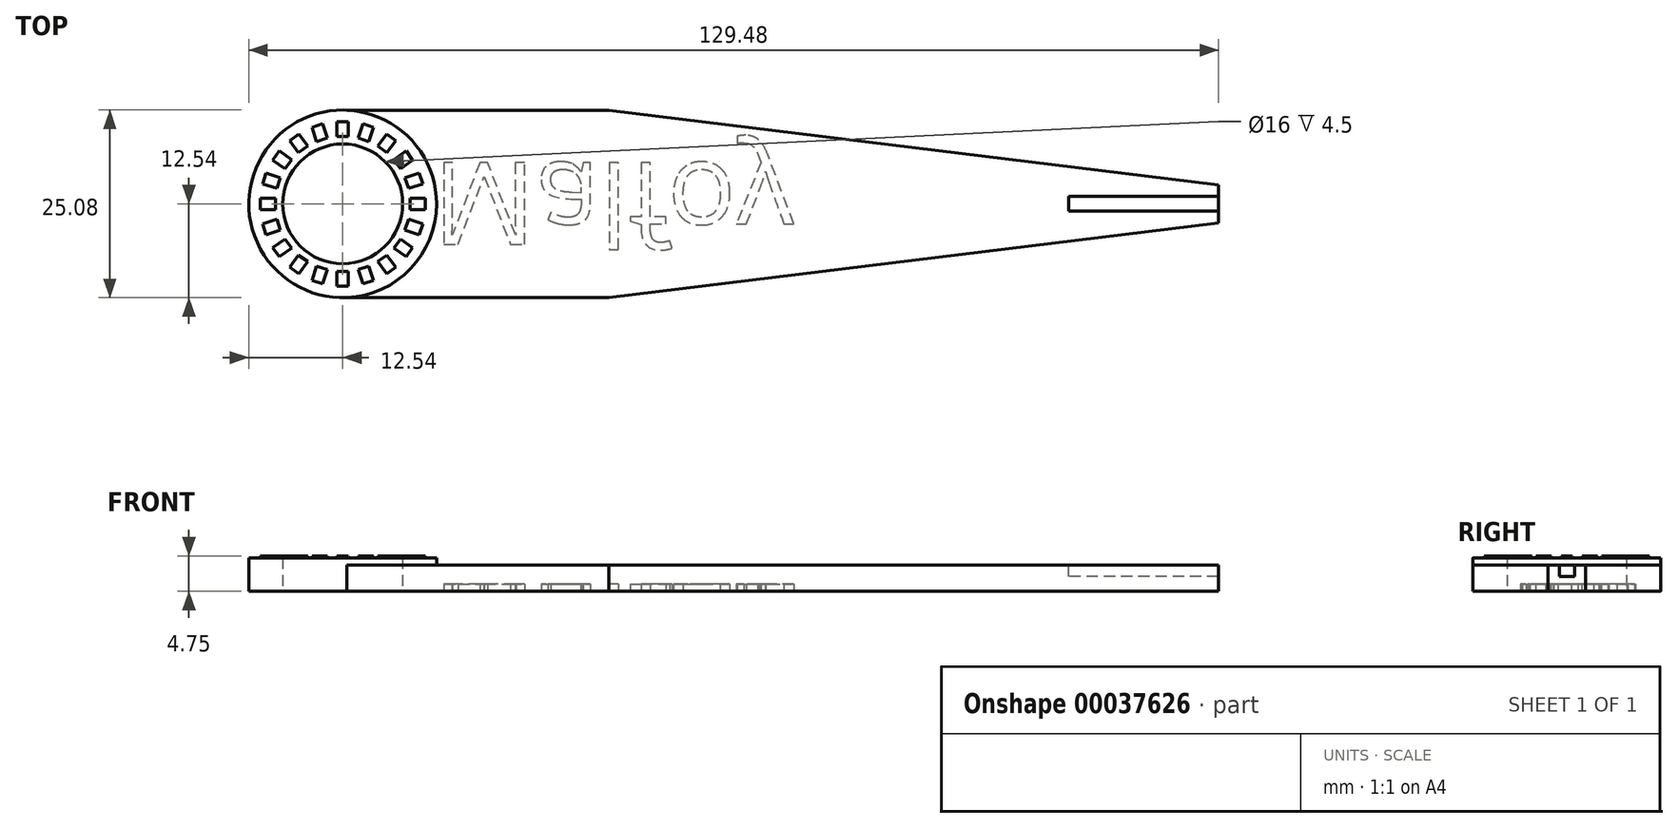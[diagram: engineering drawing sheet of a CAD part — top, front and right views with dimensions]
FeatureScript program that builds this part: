
annotation { "Feature Type Name" : "Feature", "Feature Type Description" : "" }
export const myFeature = defineFeature(function(context is Context, id is Id, definition is map)
    precondition{}
    {
        {
            var Q0;
            Q0=qCreatedBy(makeId("Top.planeOp"),FACE);
            var sketch = newSketch(context, id + "F0", { "sketchPlane" : qUnion([Q0])});
            skCircle(sketch, "E0", {"center": v(0, 0) * mm, "radius": 8 * mm});
            skLineSegment(sketch, "E1", {"start": v(35.56, 12.52) * mm, "end": v(0.56, 12.52) * mm});
            skPoint(sketch, "E2", {"position": v(0.56, 12.52) * mm});
            skLineSegment(sketch, "E3", {"start": v(0, 0) * mm, "end": v(47.57, 0) * mm, "construction": true});
            skLineSegment(sketch, "E4.MirrorCS", {"start": v(35.56, -12.52) * mm, "end": v(0.56, -12.52) * mm});
            skLineSegment(sketch, "E5", {"start": v(35.56, 12.52) * mm, "end": v(73.25, 12.52) * mm, "construction": true});
            skLineSegment(sketch, "E6", {"start": v(35.56, 12.52) * mm, "end": v(116.94, 2.53) * mm});
            skLineSegment(sketch, "E7.MirrorCS", {"start": v(35.56, -12.52) * mm, "end": v(116.94, -2.53) * mm});
            skLineSegment(sketch, "E8", {"start": v(116.94, 2.53) * mm, "end": v(116.94, -2.53) * mm});
            skArc(sketch, "E9", {"start": v(0.56, 12.52) * mm, "mid": v(-12.54, 0) * mm, "end": v(0.56, -12.52) * mm});
            skSolve(sketch);
        }
        {
            var Q0;
            Q0 = qSketchRegion(id + "F0", true);
            extrude(context, id + "F1", {"entities" : qUnion([Q0]), "depth" : 3.5 * mm});
        }
        {
            var Q0;
            Q0=makeQuery(id+"F1.opExtrude","CAP_FACE",FACE,{"disambiguationData":[OSD([sQuery(id+"F0.wireOp",EDGE,"E0"),sQuery(id+"F0.wireOp",EDGE,"E1"),sQuery(id+"F0.wireOp",EDGE,"E4.MirrorCS"),sQuery(id+"F0.wireOp",EDGE,"E6"),sQuery(id+"F0.wireOp",EDGE,"E7.MirrorCS"),sQuery(id+"F0.wireOp",EDGE,"E8"),sQuery(id+"F0.wireOp",EDGE,"E9")])],"isStart":false});
            var sketch = newSketch(context, id + "F2", { "sketchPlane" : qUnion([Q0])});
            skCircle(sketch, "E10", {"center": v(0, 0) * mm, "radius": 8 * mm});
            skCircle(sketch, "E11", {"center": v(0, 0) * mm, "radius": 12.54 * mm});
            skSolve(sketch);
        }
        {
            var Q0;
            Q0=makeQuery(id+"F2.imprint","IMPRINT",FACE,{"disambiguationData":[TD([[makeQuery(id+"F2.imprint","IMPRINT",EDGE,{"derivedFrom":sQuery(id+"F2.wireOp",EDGE,"E10")}),-1.0]])]});
            extrude(context, id + "F3", {"entities" : qUnion([Q0]), "operationType" : NewBodyOperationType.ADD, "depth" : 1 * mm});
        }
        {
            var Q0;
            Q0=makeQuery(id+"F3.opExtrude","CAP_FACE",FACE,{"disambiguationData":[OSD([sQuery(id+"F2.wireOp",EDGE,"E10"),sQuery(id+"F2.wireOp",EDGE,"E11")])],"isStart":false});
            var sketch = newSketch(context, id + "F4", { "sketchPlane" : qUnion([Q0])});
            skLineSegment(sketch, "E12.bottom", {"start": v(-0.75, 11) * mm, "end": v(0.75, 11) * mm});
            skLineSegment(sketch, "E12.top", {"start": v(-0.75, 9) * mm, "end": v(0.75, 9) * mm});
            skLineSegment(sketch, "E12.left", {"start": v(-0.75, 11) * mm, "end": v(-0.75, 9) * mm});
            skLineSegment(sketch, "E12.right", {"start": v(0.75, 11) * mm, "end": v(0.75, 9) * mm});
            skPoint(sketch, "E13", {"position": v(0, 8) * mm});
            skLineSegment(sketch, "E14.1.0", {"start": v(-4.11, 10.23) * mm, "end": v(-2.69, 10.7) * mm});
            skLineSegment(sketch, "E14.1.1", {"start": v(-4.11, 10.23) * mm, "end": v(-3.5, 8.33) * mm});
            skLineSegment(sketch, "E14.1.2", {"start": v(-3.5, 8.33) * mm, "end": v(-2.07, 8.8) * mm});
            skLineSegment(sketch, "E14.1.3", {"start": v(-2.69, 10.7) * mm, "end": v(-2.07, 8.8) * mm});
            skLineSegment(sketch, "E14.2.0", {"start": v(-7.07, 8.46) * mm, "end": v(-5.86, 9.34) * mm});
            skLineSegment(sketch, "E14.2.1", {"start": v(-7.07, 8.46) * mm, "end": v(-5.9, 6.84) * mm});
            skLineSegment(sketch, "E14.2.2", {"start": v(-5.9, 6.84) * mm, "end": v(-4.68, 7.72) * mm});
            skLineSegment(sketch, "E14.2.3", {"start": v(-5.86, 9.34) * mm, "end": v(-4.68, 7.72) * mm});
            skLineSegment(sketch, "E14.3.0", {"start": v(-9.34, 5.86) * mm, "end": v(-8.46, 7.07) * mm});
            skLineSegment(sketch, "E14.3.1", {"start": v(-9.34, 5.86) * mm, "end": v(-7.72, 4.68) * mm});
            skLineSegment(sketch, "E14.3.2", {"start": v(-7.72, 4.68) * mm, "end": v(-6.84, 5.9) * mm});
            skLineSegment(sketch, "E14.3.3", {"start": v(-8.46, 7.07) * mm, "end": v(-6.84, 5.9) * mm});
            skLineSegment(sketch, "E14.4.0", {"start": v(-10.7, 2.69) * mm, "end": v(-10.23, 4.11) * mm});
            skLineSegment(sketch, "E14.4.1", {"start": v(-10.7, 2.69) * mm, "end": v(-8.8, 2.07) * mm});
            skLineSegment(sketch, "E14.4.2", {"start": v(-8.8, 2.07) * mm, "end": v(-8.33, 3.5) * mm});
            skLineSegment(sketch, "E14.4.3", {"start": v(-10.23, 4.11) * mm, "end": v(-8.33, 3.5) * mm});
            skLineSegment(sketch, "E14.5.0", {"start": v(-11, -0.75) * mm, "end": v(-11, 0.75) * mm});
            skLineSegment(sketch, "E14.5.1", {"start": v(-11, -0.75) * mm, "end": v(-9, -0.75) * mm});
            skLineSegment(sketch, "E14.5.2", {"start": v(-9, -0.75) * mm, "end": v(-9, 0.75) * mm});
            skLineSegment(sketch, "E14.5.3", {"start": v(-11, 0.75) * mm, "end": v(-9, 0.75) * mm});
            skLineSegment(sketch, "E14.6.0", {"start": v(-10.23, -4.11) * mm, "end": v(-10.7, -2.69) * mm});
            skLineSegment(sketch, "E14.6.1", {"start": v(-10.23, -4.11) * mm, "end": v(-8.33, -3.5) * mm});
            skLineSegment(sketch, "E14.6.2", {"start": v(-8.33, -3.5) * mm, "end": v(-8.8, -2.07) * mm});
            skLineSegment(sketch, "E14.6.3", {"start": v(-10.7, -2.69) * mm, "end": v(-8.8, -2.07) * mm});
            skLineSegment(sketch, "E14.7.0", {"start": v(-8.46, -7.07) * mm, "end": v(-9.34, -5.86) * mm});
            skLineSegment(sketch, "E14.7.1", {"start": v(-8.46, -7.07) * mm, "end": v(-6.84, -5.9) * mm});
            skLineSegment(sketch, "E14.7.2", {"start": v(-6.84, -5.9) * mm, "end": v(-7.72, -4.68) * mm});
            skLineSegment(sketch, "E14.7.3", {"start": v(-9.34, -5.86) * mm, "end": v(-7.72, -4.68) * mm});
            skLineSegment(sketch, "E14.8.0", {"start": v(-5.86, -9.34) * mm, "end": v(-7.07, -8.46) * mm});
            skLineSegment(sketch, "E14.8.1", {"start": v(-5.86, -9.34) * mm, "end": v(-4.68, -7.72) * mm});
            skLineSegment(sketch, "E14.8.2", {"start": v(-4.68, -7.72) * mm, "end": v(-5.9, -6.84) * mm});
            skLineSegment(sketch, "E14.8.3", {"start": v(-7.07, -8.46) * mm, "end": v(-5.9, -6.84) * mm});
            skLineSegment(sketch, "E14.9.0", {"start": v(-2.69, -10.7) * mm, "end": v(-4.11, -10.23) * mm});
            skLineSegment(sketch, "E14.9.1", {"start": v(-2.69, -10.7) * mm, "end": v(-2.07, -8.8) * mm});
            skLineSegment(sketch, "E14.9.2", {"start": v(-2.07, -8.8) * mm, "end": v(-3.5, -8.33) * mm});
            skLineSegment(sketch, "E14.9.3", {"start": v(-4.11, -10.23) * mm, "end": v(-3.5, -8.33) * mm});
            skLineSegment(sketch, "E14.10.0", {"start": v(0.75, -11) * mm, "end": v(-0.75, -11) * mm});
            skLineSegment(sketch, "E14.10.1", {"start": v(0.75, -11) * mm, "end": v(0.75, -9) * mm});
            skLineSegment(sketch, "E14.10.2", {"start": v(0.75, -9) * mm, "end": v(-0.75, -9) * mm});
            skLineSegment(sketch, "E14.10.3", {"start": v(-0.75, -11) * mm, "end": v(-0.75, -9) * mm});
            skLineSegment(sketch, "E14.11.0", {"start": v(4.11, -10.23) * mm, "end": v(2.69, -10.7) * mm});
            skLineSegment(sketch, "E14.11.1", {"start": v(4.11, -10.23) * mm, "end": v(3.5, -8.33) * mm});
            skLineSegment(sketch, "E14.11.2", {"start": v(3.5, -8.33) * mm, "end": v(2.07, -8.8) * mm});
            skLineSegment(sketch, "E14.11.3", {"start": v(2.69, -10.7) * mm, "end": v(2.07, -8.8) * mm});
            skLineSegment(sketch, "E14.12.0", {"start": v(7.07, -8.46) * mm, "end": v(5.86, -9.34) * mm});
            skLineSegment(sketch, "E14.12.1", {"start": v(7.07, -8.46) * mm, "end": v(5.9, -6.84) * mm});
            skLineSegment(sketch, "E14.12.2", {"start": v(5.9, -6.84) * mm, "end": v(4.68, -7.72) * mm});
            skLineSegment(sketch, "E14.12.3", {"start": v(5.86, -9.34) * mm, "end": v(4.68, -7.72) * mm});
            skLineSegment(sketch, "E14.13.0", {"start": v(9.34, -5.86) * mm, "end": v(8.46, -7.07) * mm});
            skLineSegment(sketch, "E14.13.1", {"start": v(9.34, -5.86) * mm, "end": v(7.72, -4.68) * mm});
            skLineSegment(sketch, "E14.13.2", {"start": v(7.72, -4.68) * mm, "end": v(6.84, -5.9) * mm});
            skLineSegment(sketch, "E14.13.3", {"start": v(8.46, -7.07) * mm, "end": v(6.84, -5.9) * mm});
            skLineSegment(sketch, "E14.14.0", {"start": v(10.7, -2.69) * mm, "end": v(10.23, -4.11) * mm});
            skLineSegment(sketch, "E14.14.1", {"start": v(10.7, -2.69) * mm, "end": v(8.8, -2.07) * mm});
            skLineSegment(sketch, "E14.14.2", {"start": v(8.8, -2.07) * mm, "end": v(8.33, -3.5) * mm});
            skLineSegment(sketch, "E14.14.3", {"start": v(10.23, -4.11) * mm, "end": v(8.33, -3.5) * mm});
            skLineSegment(sketch, "E14.15.0", {"start": v(11, 0.75) * mm, "end": v(11, -0.75) * mm});
            skLineSegment(sketch, "E14.15.1", {"start": v(11, 0.75) * mm, "end": v(9, 0.75) * mm});
            skLineSegment(sketch, "E14.15.2", {"start": v(9, 0.75) * mm, "end": v(9, -0.75) * mm});
            skLineSegment(sketch, "E14.15.3", {"start": v(11, -0.75) * mm, "end": v(9, -0.75) * mm});
            skLineSegment(sketch, "E14.16.0", {"start": v(10.23, 4.11) * mm, "end": v(10.7, 2.69) * mm});
            skLineSegment(sketch, "E14.16.1", {"start": v(10.23, 4.11) * mm, "end": v(8.33, 3.5) * mm});
            skLineSegment(sketch, "E14.16.2", {"start": v(8.33, 3.5) * mm, "end": v(8.8, 2.07) * mm});
            skLineSegment(sketch, "E14.16.3", {"start": v(10.7, 2.69) * mm, "end": v(8.8, 2.07) * mm});
            skLineSegment(sketch, "E14.17.0", {"start": v(8.46, 7.07) * mm, "end": v(9.34, 5.86) * mm});
            skLineSegment(sketch, "E14.17.1", {"start": v(8.46, 7.07) * mm, "end": v(6.84, 5.9) * mm});
            skLineSegment(sketch, "E14.17.2", {"start": v(6.84, 5.9) * mm, "end": v(7.72, 4.68) * mm});
            skLineSegment(sketch, "E14.17.3", {"start": v(9.34, 5.86) * mm, "end": v(7.72, 4.68) * mm});
            skLineSegment(sketch, "E14.18.0", {"start": v(5.86, 9.34) * mm, "end": v(7.07, 8.46) * mm});
            skLineSegment(sketch, "E14.18.1", {"start": v(5.86, 9.34) * mm, "end": v(4.68, 7.72) * mm});
            skLineSegment(sketch, "E14.18.2", {"start": v(4.68, 7.72) * mm, "end": v(5.9, 6.84) * mm});
            skLineSegment(sketch, "E14.18.3", {"start": v(7.07, 8.46) * mm, "end": v(5.9, 6.84) * mm});
            skLineSegment(sketch, "E14.19.0", {"start": v(2.69, 10.7) * mm, "end": v(4.11, 10.23) * mm});
            skLineSegment(sketch, "E14.19.1", {"start": v(2.69, 10.7) * mm, "end": v(2.07, 8.8) * mm});
            skLineSegment(sketch, "E14.19.2", {"start": v(2.07, 8.8) * mm, "end": v(3.5, 8.33) * mm});
            skLineSegment(sketch, "E14.19.3", {"start": v(4.11, 10.23) * mm, "end": v(3.5, 8.33) * mm});
            skPoint(sketch, "E14.center", {"position": v(0, 0) * mm});
            skSolve(sketch);
        }
        {
            var Q0;
            Q0=makeQuery(id+"F4.imprint","IMPRINT",FACE,{"disambiguationData":[TD([[makeQuery(id+"F4.imprint","IMPRINT",EDGE,{"derivedFrom":sQuery(id+"F4.wireOp",EDGE,"E14.1.0")}),-1.0]])]});
            var Q1;
            Q1=makeQuery(id+"F4.imprint","IMPRINT",FACE,{"disambiguationData":[TD([[makeQuery(id+"F4.imprint","IMPRINT",EDGE,{"derivedFrom":sQuery(id+"F4.wireOp",EDGE,"E12.bottom")}),-1.0]])]});
            var Q2;
            Q2=makeQuery(id+"F4.imprint","IMPRINT",FACE,{"disambiguationData":[TD([[makeQuery(id+"F4.imprint","IMPRINT",EDGE,{"derivedFrom":sQuery(id+"F4.wireOp",EDGE,"E14.19.0")}),-1.0]])]});
            var Q3;
            Q3=makeQuery(id+"F4.imprint","IMPRINT",FACE,{"disambiguationData":[TD([[makeQuery(id+"F4.imprint","IMPRINT",EDGE,{"derivedFrom":sQuery(id+"F4.wireOp",EDGE,"E14.18.0")}),-1.0]])]});
            var Q4;
            Q4=makeQuery(id+"F4.imprint","IMPRINT",FACE,{"disambiguationData":[TD([[makeQuery(id+"F4.imprint","IMPRINT",EDGE,{"derivedFrom":sQuery(id+"F4.wireOp",EDGE,"E14.17.0")}),-1.0]])]});
            var Q5;
            Q5=makeQuery(id+"F4.imprint","IMPRINT",FACE,{"disambiguationData":[TD([[makeQuery(id+"F4.imprint","IMPRINT",EDGE,{"derivedFrom":sQuery(id+"F4.wireOp",EDGE,"E14.16.0")}),-1.0]])]});
            var Q6;
            Q6=makeQuery(id+"F4.imprint","IMPRINT",FACE,{"disambiguationData":[TD([[makeQuery(id+"F4.imprint","IMPRINT",EDGE,{"derivedFrom":sQuery(id+"F4.wireOp",EDGE,"E14.15.0")}),-1.0]])]});
            var Q7;
            Q7=makeQuery(id+"F4.imprint","IMPRINT",FACE,{"disambiguationData":[TD([[makeQuery(id+"F4.imprint","IMPRINT",EDGE,{"derivedFrom":sQuery(id+"F4.wireOp",EDGE,"E14.14.0")}),-1.0]])]});
            var Q8;
            Q8=makeQuery(id+"F4.imprint","IMPRINT",FACE,{"disambiguationData":[TD([[makeQuery(id+"F4.imprint","IMPRINT",EDGE,{"derivedFrom":sQuery(id+"F4.wireOp",EDGE,"E14.13.0")}),-1.0]])]});
            var Q9;
            Q9=makeQuery(id+"F4.imprint","IMPRINT",FACE,{"disambiguationData":[TD([[makeQuery(id+"F4.imprint","IMPRINT",EDGE,{"derivedFrom":sQuery(id+"F4.wireOp",EDGE,"E14.12.0")}),-1.0]])]});
            var Q10;
            Q10=makeQuery(id+"F4.imprint","IMPRINT",FACE,{"disambiguationData":[TD([[makeQuery(id+"F4.imprint","IMPRINT",EDGE,{"derivedFrom":sQuery(id+"F4.wireOp",EDGE,"E14.11.0")}),-1.0]])]});
            var Q11;
            Q11=makeQuery(id+"F4.imprint","IMPRINT",FACE,{"disambiguationData":[TD([[makeQuery(id+"F4.imprint","IMPRINT",EDGE,{"derivedFrom":sQuery(id+"F4.wireOp",EDGE,"E14.10.0")}),-1.0]])]});
            var Q12;
            Q12=makeQuery(id+"F4.imprint","IMPRINT",FACE,{"disambiguationData":[TD([[makeQuery(id+"F4.imprint","IMPRINT",EDGE,{"derivedFrom":sQuery(id+"F4.wireOp",EDGE,"E14.9.0")}),-1.0]])]});
            var Q13;
            Q13=makeQuery(id+"F4.imprint","IMPRINT",FACE,{"disambiguationData":[TD([[makeQuery(id+"F4.imprint","IMPRINT",EDGE,{"derivedFrom":sQuery(id+"F4.wireOp",EDGE,"E14.8.0")}),-1.0]])]});
            var Q14;
            Q14=makeQuery(id+"F4.imprint","IMPRINT",FACE,{"disambiguationData":[TD([[makeQuery(id+"F4.imprint","IMPRINT",EDGE,{"derivedFrom":sQuery(id+"F4.wireOp",EDGE,"E14.7.0")}),-1.0]])]});
            var Q15;
            Q15=makeQuery(id+"F4.imprint","IMPRINT",FACE,{"disambiguationData":[TD([[makeQuery(id+"F4.imprint","IMPRINT",EDGE,{"derivedFrom":sQuery(id+"F4.wireOp",EDGE,"E14.6.0")}),-1.0]])]});
            var Q16;
            Q16=makeQuery(id+"F4.imprint","IMPRINT",FACE,{"disambiguationData":[TD([[makeQuery(id+"F4.imprint","IMPRINT",EDGE,{"derivedFrom":sQuery(id+"F4.wireOp",EDGE,"E14.5.0")}),-1.0]])]});
            var Q17;
            Q17=makeQuery(id+"F4.imprint","IMPRINT",FACE,{"disambiguationData":[TD([[makeQuery(id+"F4.imprint","IMPRINT",EDGE,{"derivedFrom":sQuery(id+"F4.wireOp",EDGE,"E14.4.0")}),-1.0]])]});
            var Q18;
            Q18=makeQuery(id+"F4.imprint","IMPRINT",FACE,{"disambiguationData":[TD([[makeQuery(id+"F4.imprint","IMPRINT",EDGE,{"derivedFrom":sQuery(id+"F4.wireOp",EDGE,"E14.3.0")}),-1.0]])]});
            var Q19;
            Q19=makeQuery(id+"F4.imprint","IMPRINT",FACE,{"disambiguationData":[TD([[makeQuery(id+"F4.imprint","IMPRINT",EDGE,{"derivedFrom":sQuery(id+"F4.wireOp",EDGE,"E14.2.0")}),-1.0]])]});
            extrude(context, id + "F5", {"entities" : qUnion([Q0, Q1, Q2, Q3, Q4, Q5, Q6, Q7, Q8, Q9, Q10, Q11, Q12, Q13, Q14, Q15, Q16, Q17, Q18, Q19]), "operationType" : NewBodyOperationType.ADD, "depth" : .25 * mm});
        }
        {
            var Q0;
            Q0=makeQuery(id+"F1.opExtrude","CAP_FACE",FACE,{"disambiguationData":[OSD([sQuery(id+"F0.wireOp",EDGE,"E0"),sQuery(id+"F0.wireOp",EDGE,"E1"),sQuery(id+"F0.wireOp",EDGE,"E4.MirrorCS"),sQuery(id+"F0.wireOp",EDGE,"E6"),sQuery(id+"F0.wireOp",EDGE,"E7.MirrorCS"),sQuery(id+"F0.wireOp",EDGE,"E8"),sQuery(id+"F0.wireOp",EDGE,"E9")])],"isStart":false});
            var sketch = newSketch(context, id + "F6", { "sketchPlane" : qUnion([Q0])});
            skLineSegment(sketch, "E15.bottom", {"start": v(116.94, 1.03) * mm, "end": v(96.94, 1.03) * mm});
            skLineSegment(sketch, "E15.top", {"start": v(116.94, -0.97) * mm, "end": v(96.94, -0.97) * mm});
            skLineSegment(sketch, "E15.left", {"start": v(116.94, 1.03) * mm, "end": v(116.94, -0.97) * mm});
            skLineSegment(sketch, "E15.right", {"start": v(96.94, 1.03) * mm, "end": v(96.94, -0.97) * mm});
            skSolve(sketch);
        }
        {
            var Q0;
            Q0 = qSketchRegion(id + "F6", true);
            extrude(context, id + "F7", {"entities" : qUnion([Q0]), "operationType" : NewBodyOperationType.REMOVE, "oppositeDirection" : true, "depth" : 1.5 * mm});
        }
        {
            var Q0;
            Q0=qCreatedBy(makeId("Top.planeOp"),FACE);
            var Q1;
            Q1=sQuery(id+"F0.wireOp",EDGE,"E1");
            cPlane(context, id + "F8", {"entities" : qUnion([Q0, Q1]), "cplaneType" : CPlaneType.LINE_ANGLE, "offset" : 150 * mm, "angle" : 0 * degree, "width" : 150 * mm, "height" : 150 * mm});
        }
        {
            var Q0;
            Q0=qCreatedBy(id+"F8.planeOp",FACE);
            var sketch = newSketch(context, id + "F9", { "sketchPlane" : qUnion([Q0])});
            skText(sketch, "E16", { "text": "Malfoy", "fontName": "OpenSans-Regular.ttf"});
            skPoint(sketch, "E17", {"position": v(12, 0) * mm});
            const initialGuessF9  = {"E16": [0.012, -0.0055, 1, 0, 0.011]};
            skSetInitialGuess(sketch, initialGuessF9);
            skSolve(sketch);
        }
        {
            var Q0;
            Q0 = qSketchRegion(id + "F9", true);
            extrude(context, id + "F10", {"entities" : qUnion([Q0]), "operationType" : NewBodyOperationType.REMOVE, "oppositeDirection" : true, "depth" : 1 * mm});
        }
    });
